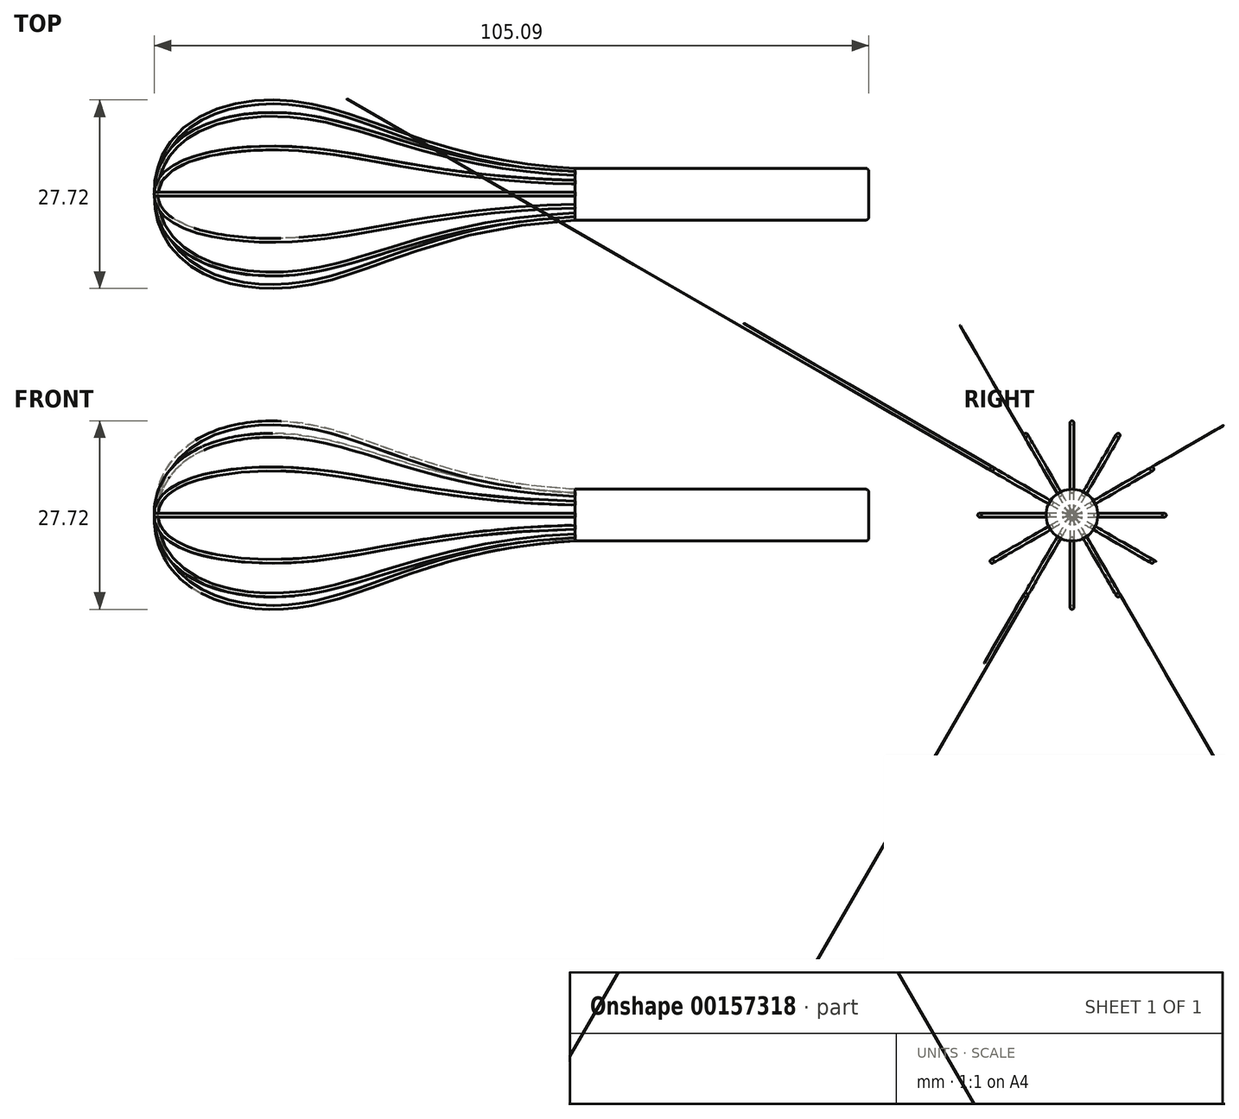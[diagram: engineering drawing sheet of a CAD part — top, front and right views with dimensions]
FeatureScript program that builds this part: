
annotation { "Feature Type Name" : "Feature", "Feature Type Description" : "" }
export const myFeature = defineFeature(function(context is Context, id is Id, definition is map)
    precondition{}
    {
        {
            var Q0;
            Q0=qCreatedBy(makeId("Right.planeOp"),FACE);
            var sketch = newSketch(context, id + "F0", { "sketchPlane" : qUnion([Q0])});
            skCircle(sketch, "E0", {"center": v(0, 0) * mm, "radius": 3.8 * mm});
            skSolve(sketch);
        }
        {
            var Q0;
            Q0=makeQuery(id+"F0.imprint","IMPRINT",FACE,{"disambiguationData":[TD([[makeQuery(id+"F0.imprint","IMPRINT",EDGE,{"derivedFrom":sQuery(id+"F0.wireOp",EDGE,"E0")}),1.0]])]});
            extrude(context, id + "F1", {"entities" : qUnion([Q0]), "depth" : 43.18 * mm});
        }
        {
            var Q0;
            Q0=qCreatedBy(makeId("Front.planeOp"),FACE);
            var sketch = newSketch(context, id + "F2", { "sketchPlane" : qUnion([Q0])});
            skFitSpline(sketch, "E1", {"points": [v(0, 2.86) * mm, v(-42.86, 12.86) * mm, v(-60.96, 0) * mm], "startDerivative": vector(-113.87, 5.86) * mm, "endDerivative": vector(0, -72.94) * mm});
            skFitSpline(sketch, "E2.MirrorCS", {"points": [v(0, -2.86) * mm, v(-42.86, -12.86) * mm, v(-60.96, 0) * mm], "startDerivative": vector(-113.87, -5.86) * mm, "endDerivative": vector(0, 72.94) * mm});
            skSolve(sketch);
        }
        {
            var Q0;
            Q0=qCreatedBy(makeId("Right.planeOp"),FACE);
            var sketch = newSketch(context, id + "F3", { "sketchPlane" : qUnion([Q0])});
            skCircle(sketch, "E3", {"center": v(0, 3.52) * mm, "radius": 0.29 * mm});
            skCircle(sketch, "E4", {"center": v(-3.52, 0) * mm, "radius": 0.29 * mm});
            skCircle(sketch, "E5", {"center": v(-2.5, 2.5) * mm, "radius": 0.29 * mm});
            skLineSegment(sketch, "E6", {"start": v(-2.5, 0) * mm, "end": v(-2.5, 2.5) * mm, "construction": true});
            skLineSegment(sketch, "E7", {"start": v(-2.5, 2.5) * mm, "end": v(0, 2.5) * mm, "construction": true});
            skCircle(sketch, "E8.MirrorC", {"center": v(-2.5, -2.5) * mm, "radius": 0.29 * mm});
            skSolve(sketch);
        }
        {
            var Q0;
            Q0=makeQuery(id+"F3.imprint","IMPRINT",FACE,{"disambiguationData":[TD([[makeQuery(id+"F3.imprint","IMPRINT",EDGE,{"derivedFrom":sQuery(id+"F3.wireOp",EDGE,"E3")}),1.0]])]});
            var Q1;
            Q1=sQuery(id+"F2.wireOp",EDGE,"E1");
            var Q2;
            Q2=sQuery(id+"F2.wireOp",EDGE,"E2.MirrorCS");
            sweep(context, id + "F4", {"profiles" : qUnion([Q0]), "path" : qUnion([Q1, Q2])});
        }
        {
            var Q0;
            Q0=makeQuery(id+"F4.opSweep","SWEPT_BODY",BODY,{"disambiguationData":[OSD([sQuery(id+"F2.wireOp",EDGE,"E2.MirrorCS"),sQuery(id+"F3.wireOp",EDGE,"E3")])]});
            var Q1;
            Q1=sQuery(id+"F0.wireOp",EDGE,"E0");
            circularPattern(context, id + "F5", {"entities" : qUnion([Q0]), "axis" : qUnion([Q1]), "angle" : 30 * degree, "instanceCount" : 8});
        }
        {
            var Q0;
            Q0=makeQuery(id+"F1.opExtrude","CAP_EDGE",EDGE,{"disambiguationData":[OSD([sQuery(id+"F0.wireOp",EDGE,"E0")])],"isStart":false});
            fillet(context, id + "F6", {"entities" : qUnion([Q0]), "radius" : 0.5 * mm, "tangentPropagation" : true, "allowEdgeOverflow" : false});
        }
    });
